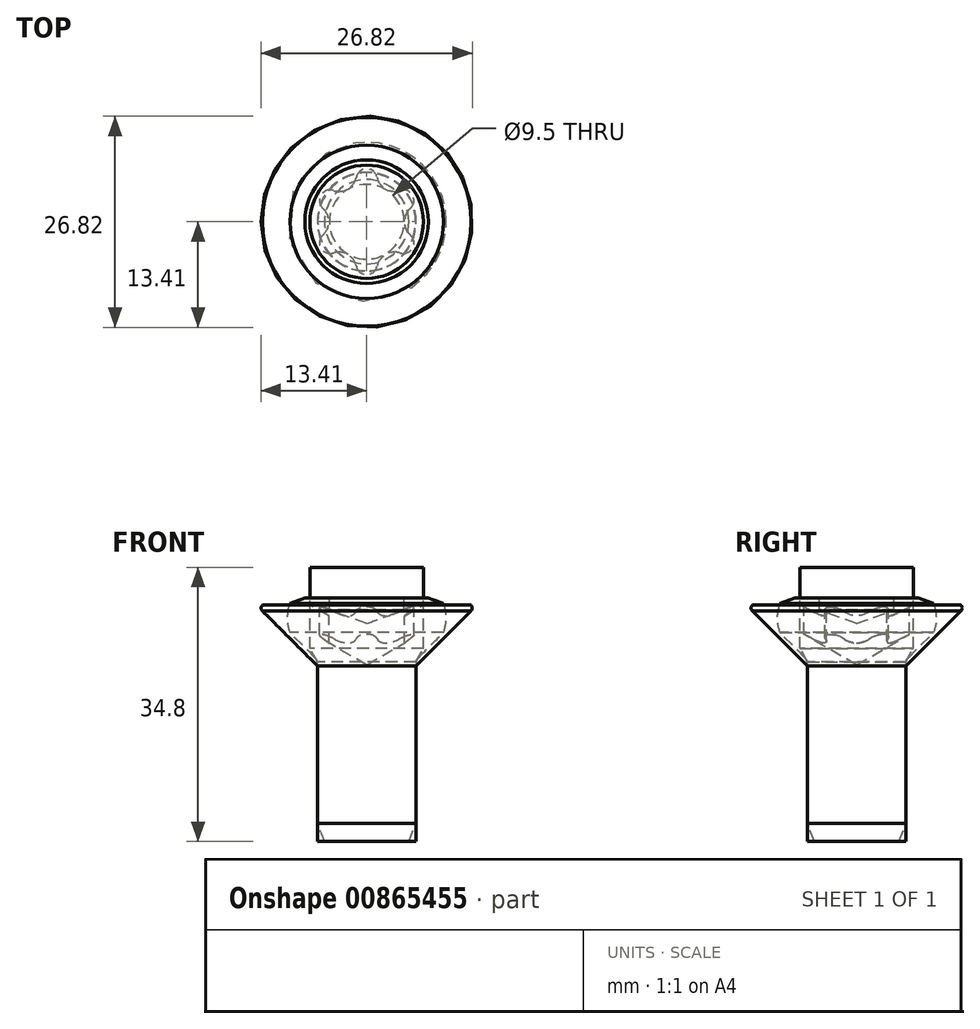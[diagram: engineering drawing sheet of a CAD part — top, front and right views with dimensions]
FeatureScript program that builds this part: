
annotation { "Feature Type Name" : "Feature", "Feature Type Description" : "" }
export const myFeature = defineFeature(function(context is Context, id is Id, definition is map)
    precondition{}
    {
        {
            var Q0;
            Q0=qCreatedBy(makeId("Front.planeOp"),FACE);
            var sketch = newSketch(context, id + "F0", { "sketchPlane" : qUnion([Q0])});
            skLineSegment(sketch, "E0", {"start": v(0, 0) * mm, "end": v(0, 22.42) * mm});
            skLineSegment(sketch, "E1", {"start": v(6.72, 30) * mm, "end": v(13.25, 30) * mm});
            skLineSegment(sketch, "E2", {"start": v(13.25, 29.28) * mm, "end": v(6.27, 22.3) * mm});
            skLineSegment(sketch, "E3", {"start": v(6.27, 22.3) * mm, "end": v(6.28, 2.29) * mm});
            skLineSegment(sketch, "E4", {"start": v(6.28, 2.29) * mm, "end": v(5.35, 0) * mm});
            skLineSegment(sketch, "E5", {"start": v(5.35, 0) * mm, "end": v(0, 0) * mm});
            skLineSegment(sketch, "E6", {"start": v(0, 22.42) * mm, "end": v(0, 0) * mm, "construction": true});
            skLineSegment(sketch, "E7", {"start": v(6.72, 30) * mm, "end": v(6.72, 26.3) * mm});
            skLineSegment(sketch, "E8", {"start": v(6.72, 26.3) * mm, "end": v(0, 22.42) * mm});
            skArc(sketch, "E9", {"start": v(13.25, 29.28) * mm, "mid": v(13.4, 29.64) * mm, "end": v(13.25, 30) * mm});
            skSolve(sketch);
        }
        {
            var Q0;
            Q0 = qSketchRegion(id + "F0", true);
            var Q1;
            Q1=sQuery(id+"F0.wireOp",EDGE,"E0");
            revolve(context, id + "F1", {"surfaceOperationType" : NewSurfaceOperationType.NEW, "entities" : qUnion([Q0]), "axis" : qUnion([Q1]), "revolveType" : RevolveType.FULL});
        }
        {
            var Q0;
            Q0=makeQuery(id+"F1.opRevolve","SWEPT_FACE",FACE,{"disambiguationData":[OSD([sQuery(id+"F0.wireOp",EDGE,"E1")])]});
            var sketch = newSketch(context, id + "F2", { "sketchPlane" : qUnion([Q0])});
            skCircle(sketch, "E10", {"center": v(0, 0) * mm, "radius": 4.8 * mm, "construction": true});
            skCircle(sketch, "E11", {"center": v(0, 0) * mm, "radius": 6.72 * mm, "construction": true});
            skArc(sketch, "E12", {"start": v(1.32, 5.65) * mm, "mid": v(0, 6.72) * mm, "end": v(-1.32, 5.65) * mm});
            skArc(sketch, "E13", {"start": v(1.32, 5.65) * mm, "mid": v(2.4, 4.16) * mm, "end": v(4.24, 3.97) * mm});
            skArc(sketch, "E14.1.0", {"start": v(-4.24, 3.97) * mm, "mid": v(-5.82, 3.36) * mm, "end": v(-5.56, 1.69) * mm});
            skArc(sketch, "E14.2.0", {"start": v(-5.56, -1.69) * mm, "mid": v(-5.82, -3.36) * mm, "end": v(-4.24, -3.97) * mm});
            skArc(sketch, "E14.3.0", {"start": v(-1.32, -5.65) * mm, "mid": v(0, -6.72) * mm, "end": v(1.32, -5.65) * mm});
            skArc(sketch, "E14.4.0", {"start": v(4.24, -3.97) * mm, "mid": v(5.82, -3.36) * mm, "end": v(5.56, -1.69) * mm});
            skArc(sketch, "E14.5.0", {"start": v(5.56, 1.69) * mm, "mid": v(5.82, 3.36) * mm, "end": v(4.24, 3.97) * mm});
            skArc(sketch, "E15.1.0", {"start": v(-4.24, 3.97) * mm, "mid": v(-2.4, 4.16) * mm, "end": v(-1.32, 5.65) * mm});
            skArc(sketch, "E15.2.0", {"start": v(-5.56, -1.69) * mm, "mid": v(-4.8, 0) * mm, "end": v(-5.56, 1.69) * mm});
            skArc(sketch, "E15.3.0", {"start": v(-1.32, -5.65) * mm, "mid": v(-2.4, -4.16) * mm, "end": v(-4.24, -3.97) * mm});
            skArc(sketch, "E15.4.0", {"start": v(4.24, -3.97) * mm, "mid": v(2.4, -4.16) * mm, "end": v(1.32, -5.65) * mm});
            skArc(sketch, "E15.5.0", {"start": v(5.56, 1.69) * mm, "mid": v(4.8, 0) * mm, "end": v(5.56, -1.69) * mm});
            skCircle(sketch, "E16", {"center": v(0, 0) * mm, "radius": 8.06 * mm});
            skSolve(sketch);
        }
        {
            var Q0;
            Q0 = qSketchRegion(id + "F2", true);
            var Q1;
            Q1=makeQuery(id+"F1.opRevolve","SWEPT_FACE",FACE,{"disambiguationData":[OSD([sQuery(id+"F0.wireOp",EDGE,"E8")])]});
            extrude(context, id + "F3", {"entities" : qUnion([Q0]), "operationType" : NewBodyOperationType.ADD, "endBound" : BoundingType.UP_TO_SURFACE, "oppositeDirection" : true, "depth" : 25 * mm, "endBoundEntityFace" : qUnion([Q1]), "offsetDistance" : 25 * mm});
        }
        {
            var Q0;
            Q0=makeQuery(id+"F3.boolean.opBoolean","MERGE",FACE,{"derivedFrom":[makeQuery(id+"F1.opRevolve","SWEPT_FACE",FACE,{"disambiguationData":[OSD([sQuery(id+"F0.wireOp",EDGE,"E1")])]}),makeQuery(id+"F3.opExtrude","CAP_FACE",FACE,{"disambiguationData":[OSD([sQuery(id+"F2.wireOp",EDGE,"E12"),sQuery(id+"F2.wireOp",EDGE,"E13"),sQuery(id+"F2.wireOp",EDGE,"E14.1.0"),sQuery(id+"F2.wireOp",EDGE,"E14.2.0"),sQuery(id+"F2.wireOp",EDGE,"E14.3.0"),sQuery(id+"F2.wireOp",EDGE,"E14.4.0"),sQuery(id+"F2.wireOp",EDGE,"E14.5.0"),sQuery(id+"F2.wireOp",EDGE,"E15.1.0"),sQuery(id+"F2.wireOp",EDGE,"E15.2.0"),sQuery(id+"F2.wireOp",EDGE,"E15.3.0"),sQuery(id+"F2.wireOp",EDGE,"E15.4.0"),sQuery(id+"F2.wireOp",EDGE,"E15.5.0"),sQuery(id+"F2.wireOp",EDGE,"E16")])],"isStart":true})]});
            var sketch = newSketch(context, id + "F4", { "sketchPlane" : qUnion([Q0])});
            skCircle(sketch, "E17", {"center": v(0, 0) * mm, "radius": 7.13 * mm});
            skSolve(sketch);
        }
        {
            var Q0;
            Q0 = qSketchRegion(id + "F4", true);
            extrude(context, id + "F5", {"entities" : qUnion([Q0]), "operationType" : NewBodyOperationType.REMOVE, "oppositeDirection" : true, "depth" : 25 * mm, "offsetDistance" : 25 * mm, "hasDraft" : true, "draftAngle" : 60 * degree, "draftPullDirection" : true});
        }
        {
            var Q0;
            Q0=qCreatedBy(makeId("Front.planeOp"),FACE);
            var sketch = newSketch(context, id + "F6", { "sketchPlane" : qUnion([Q0])});
            skLineSegment(sketch, "E18", {"start": v(0, 0) * mm, "end": v(0, 27.67) * mm, "construction": true});
            skLineSegment(sketch, "E19", {"start": v(0, 27.67) * mm, "end": v(4.75, 29.4) * mm});
            skLineSegment(sketch, "E20", {"start": v(4.75, 29.4) * mm, "end": v(4.75, 30.9) * mm});
            skLineSegment(sketch, "E21", {"start": v(4.75, 30.9) * mm, "end": v(7.85, 30.9) * mm});
            skLineSegment(sketch, "E22", {"start": v(7.85, 30.9) * mm, "end": v(9.75, 30.2) * mm});
            skLineSegment(sketch, "E23", {"start": v(9.75, 26.51) * mm, "end": v(6.54, 23.3) * mm});
            skLineSegment(sketch, "E24", {"start": v(6.25, 22.6) * mm, "end": v(6.25, 0) * mm});
            skLineSegment(sketch, "E25", {"start": v(6.25, 0) * mm, "end": v(0, 0) * mm});
            skLineSegment(sketch, "E26", {"start": v(0, 27.67) * mm, "end": v(0, 0) * mm});
            skPoint(sketch, "E27.visualSharp", {"position": v(6.25, 23.01) * mm});
            skArc(sketch, "E27.filletArc", {"start": v(6.54, 23.3) * mm, "mid": v(6.33, 22.98) * mm, "end": v(6.25, 22.6) * mm});
            skArc(sketch, "E28", {"start": v(9.75, 26.51) * mm, "mid": v(10.1, 28.36) * mm, "end": v(9.75, 30.2) * mm});
            skSolve(sketch);
        }
        {
            var Q0;
            Q0 = qSketchRegion(id + "F6", true);
            var Q1;
            Q1=sQuery(id+"F6.wireOp",EDGE,"E26");
            revolve(context, id + "F7", {"surfaceOperationType" : NewSurfaceOperationType.NEW, "entities" : qUnion([Q0]), "axis" : qUnion([Q1]), "revolveType" : RevolveType.FULL});
        }
        {
            var Q0;
            Q0=qCreatedBy(makeId("Front.planeOp"),FACE);
            var sketch = newSketch(context, id + "F8", { "sketchPlane" : qUnion([Q0])});
            skLineSegment(sketch, "E29", {"start": v(0, 0) * mm, "end": v(0, 34.8) * mm, "construction": true});
            skLineSegment(sketch, "E30", {"start": v(0, 34.8) * mm, "end": v(7.2, 34.8) * mm});
            skLineSegment(sketch, "E31", {"start": v(7.2, 34.8) * mm, "end": v(7.2, 24.49) * mm});
            skLineSegment(sketch, "E32", {"start": v(7.2, 24.49) * mm, "end": v(6.22, 22.8) * mm});
            skLineSegment(sketch, "E33", {"start": v(6.22, 22.8) * mm, "end": v(6.23, 0) * mm});
            skLineSegment(sketch, "E34", {"start": v(6.23, 0) * mm, "end": v(0, 0) * mm});
            skLineSegment(sketch, "E35", {"start": v(0, 34.8) * mm, "end": v(0, 0) * mm});
            skSolve(sketch);
        }
        {
            var Q0;
            Q0 = qSketchRegion(id + "F8", true);
            var Q1;
            Q1=sQuery(id+"F8.wireOp",EDGE,"E35");
            revolve(context, id + "F9", {"surfaceOperationType" : NewSurfaceOperationType.NEW, "entities" : qUnion([Q0]), "axis" : qUnion([Q1]), "revolveType" : RevolveType.FULL});
        }
    });
